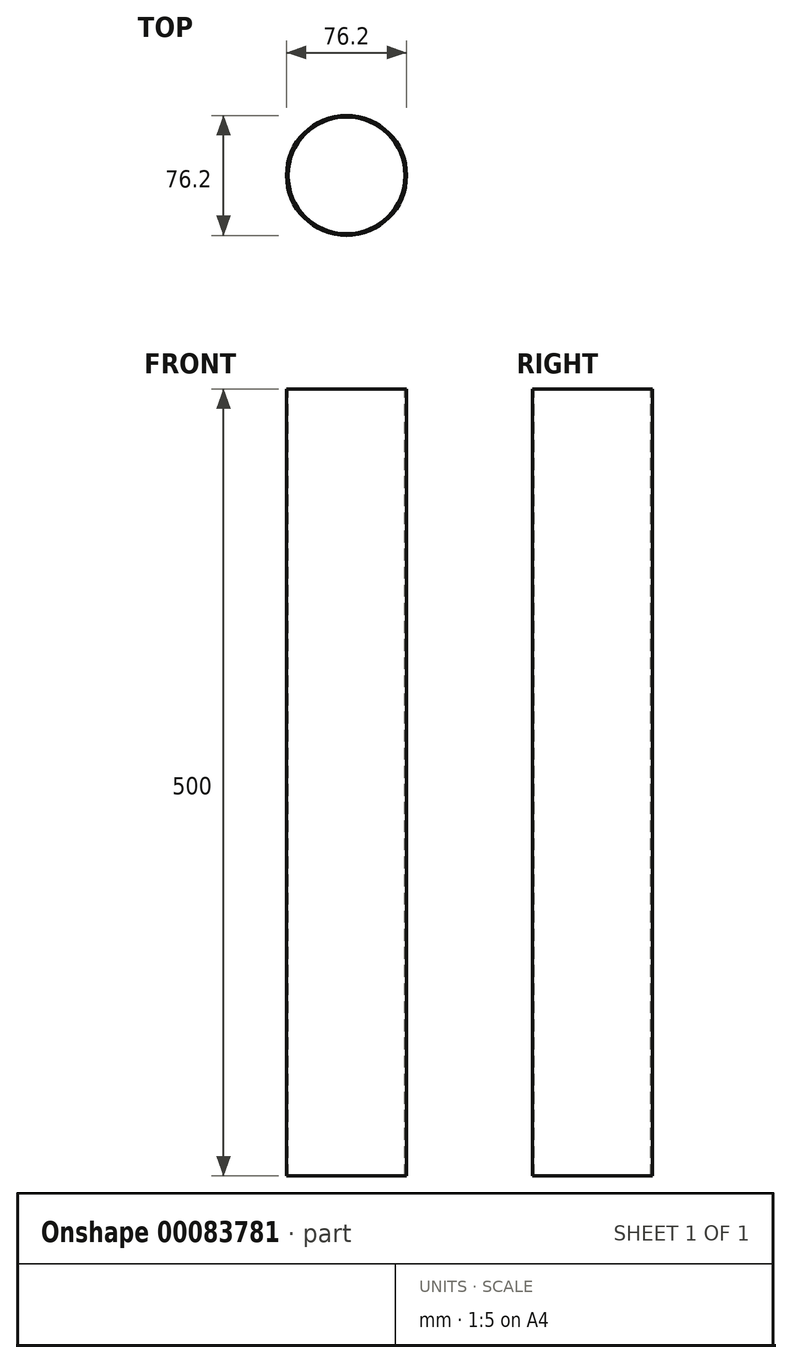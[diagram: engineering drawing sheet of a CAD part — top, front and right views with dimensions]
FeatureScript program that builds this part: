
annotation { "Feature Type Name" : "Feature", "Feature Type Description" : "" }
export const myFeature = defineFeature(function(context is Context, id is Id, definition is map)
    precondition{}
    {
        {
            var Q0;
            Q0=qCreatedBy(makeId("Top.planeOp"),FACE);
            var sketch = newSketch(context, id + "F0", { "sketchPlane" : qUnion([Q0])});
            skCircle(sketch, "E0", {"center": v(0, 0) * mm, "radius": 38.1 * mm});
            skCircle(sketch, "E1", {"center": v(0, 0) * mm, "radius": 37.1 * mm});
            skSolve(sketch);
        }
        {
            var Q0;
            Q0=sQuery(id+"F0.wireOp",EDGE,"E1");
            var Q1;
            Q1=sQuery(id+"F0.wireOp",EDGE,"E0");
            extrude(context, id + "F1", {"bodyType" : ToolBodyType.SURFACE, "surfaceEntities" : qUnion([Q0, Q1]), "depth" : 500 * mm});
        }
    });
